# Revit family: CADS_Vent-Axia_MechEquip_Fan_TDF_PowerlineTwin - EXTRACT
name_source: partatom
category: Mechanical Equipment
units: mm (PartAtom-declared; Revit-internal decimal feet)

## family parameters
Always vertical = Yes
Cut with Voids When Loaded = No
OmniClass Number = 23.75.00.00
OmniClass Title = Climate Control (HVAC)
Part Type = Normal
Room Calculation Point = No
Round Connector Dimension = Use Diameter
Shared = No
Work Plane-Based = No

## types (11) — shared parameters
AirflowRateRange = 0.0 L/s
AssemblyPlace = UNKNOWN
AssetType = FIXED
DurationUnit = Year
ExteriorInsulation = No
Fitting Type = Ignore
GrossWeight = 0.00 kg
HasProtectiveEarth = No
IfcExportAs = IfcFanType
IsExtendedWarranty = No
ManufacturerAddress = Fleming Way
Crawley 
RH10 9YX
ModelReference = POWERLINE TWIN CENTRIF IN LINE DUCT FAN
Quantity = 1
RatedCurrent = 0 A
RatedVoltage = 0 V
Status = New
WarrantyGuarantor = Vent-Axia Limited
WorkingPressure = 0.0 Pa
zero-valued in all types: CADS_Index, CADS_Usage, Default Elevation, ExpectedServiceLife, NumberOfPoles

## per-type parameters (varying)
| type | Baffle | K | L | NominalDiameter | NominalHeight | NominalLength | NominalWidth |
| TDF32014 | 490 mm  [stored 1.60761 ft] | 150 mm | 130 mm  [stored 0.426509 ft] | 320 mm  [stored 1.04987 ft] | 655 mm  [stored 2.14895 ft] | 900 mm  [stored 2.95276 ft] | 500 mm  [stored 1.64042 ft] |
| TDF38014 | 540 mm  [stored 1.77165 ft] | 160 mm  [stored 0.524934 ft] | 130 mm  [stored 0.426509 ft] | 380 mm | 745 mm  [stored 2.44423 ft] | 1015 mm  [stored 3.33005 ft] | 550 mm |
| TDF38034 | 540 mm  [stored 1.77165 ft] | 160 mm  [stored 0.524934 ft] | 130 mm  [stored 0.426509 ft] | 380 mm | 745 mm  [stored 2.44423 ft] | 1015 mm  [stored 3.33005 ft] | 550 mm |
| TDF42014 | 615 mm  [stored 2.01772 ft] | 230 mm  [stored 0.754593 ft] | 230 mm  [stored 0.754593 ft] | 420 mm  [stored 1.37795 ft] | 830 mm  [stored 2.7231 ft] | 1130 mm  [stored 3.70735 ft] | 625 mm  [stored 2.05052 ft] |
| TDF42034 | 615 mm  [stored 2.01772 ft] | 230 mm  [stored 0.754593 ft] | 230 mm  [stored 0.754593 ft] | 420 mm  [stored 1.37795 ft] | 830 mm  [stored 2.7231 ft] | 1130 mm  [stored 3.70735 ft] | 625 mm  [stored 2.05052 ft] |
| TDF48014 | 690 mm  [stored 2.26378 ft] | 230 mm  [stored 0.754593 ft] | 230 mm  [stored 0.754593 ft] | 480 mm  [stored 1.5748 ft] | 925 mm  [stored 3.03478 ft] | 1250 mm  [stored 4.10105 ft] | 700 mm  [stored 2.29659 ft] |
| TDF48034 | 690 mm  [stored 2.26378 ft] | 230 mm  [stored 0.754593 ft] | 230 mm  [stored 0.754593 ft] | 480 mm  [stored 1.5748 ft] | 925 mm  [stored 3.03478 ft] | 1250 mm  [stored 4.10105 ft] | 700 mm  [stored 2.29659 ft] |
| TDF52034 | 765 mm  [stored 2.50984 ft] | 230 mm  [stored 0.754593 ft] | 230 mm  [stored 0.754593 ft] | 520 mm  [stored 1.70604 ft] | 1055 mm  [stored 3.46129 ft] | 1385 mm  [stored 4.54396 ft] | 775 mm  [stored 2.54265 ft] |
| TDF52036 | 765 mm  [stored 2.50984 ft] | 230 mm  [stored 0.754593 ft] | 230 mm  [stored 0.754593 ft] | 520 mm  [stored 1.70604 ft] | 1055 mm  [stored 3.46129 ft] | 1385 mm  [stored 4.54396 ft] | 775 mm  [stored 2.54265 ft] |
| TDF60034 | 840 mm  [stored 2.75591 ft] | 230 mm  [stored 0.754593 ft] | 230 mm  [stored 0.754593 ft] | 600 mm | 1200 mm | 1530 mm  [stored 5.01969 ft] | 850 mm  [stored 2.78871 ft] |
| TDF60036 | 840 mm  [stored 2.75591 ft] | 230 mm  [stored 0.754593 ft] | 230 mm  [stored 0.754593 ft] | 600 mm | 1200 mm | 1530 mm  [stored 5.01969 ft] | 850 mm  [stored 2.78871 ft] |

note: column(s) folded — value = type name in every type: ModelNumber

note: [stored X ft] marks values corroborated as IEEE doubles in the binary element streams (Revit-internal decimal feet)

## geometry (parser evidence)
native form markers: Sweep x3
no freeform markers — native parametric forms only
